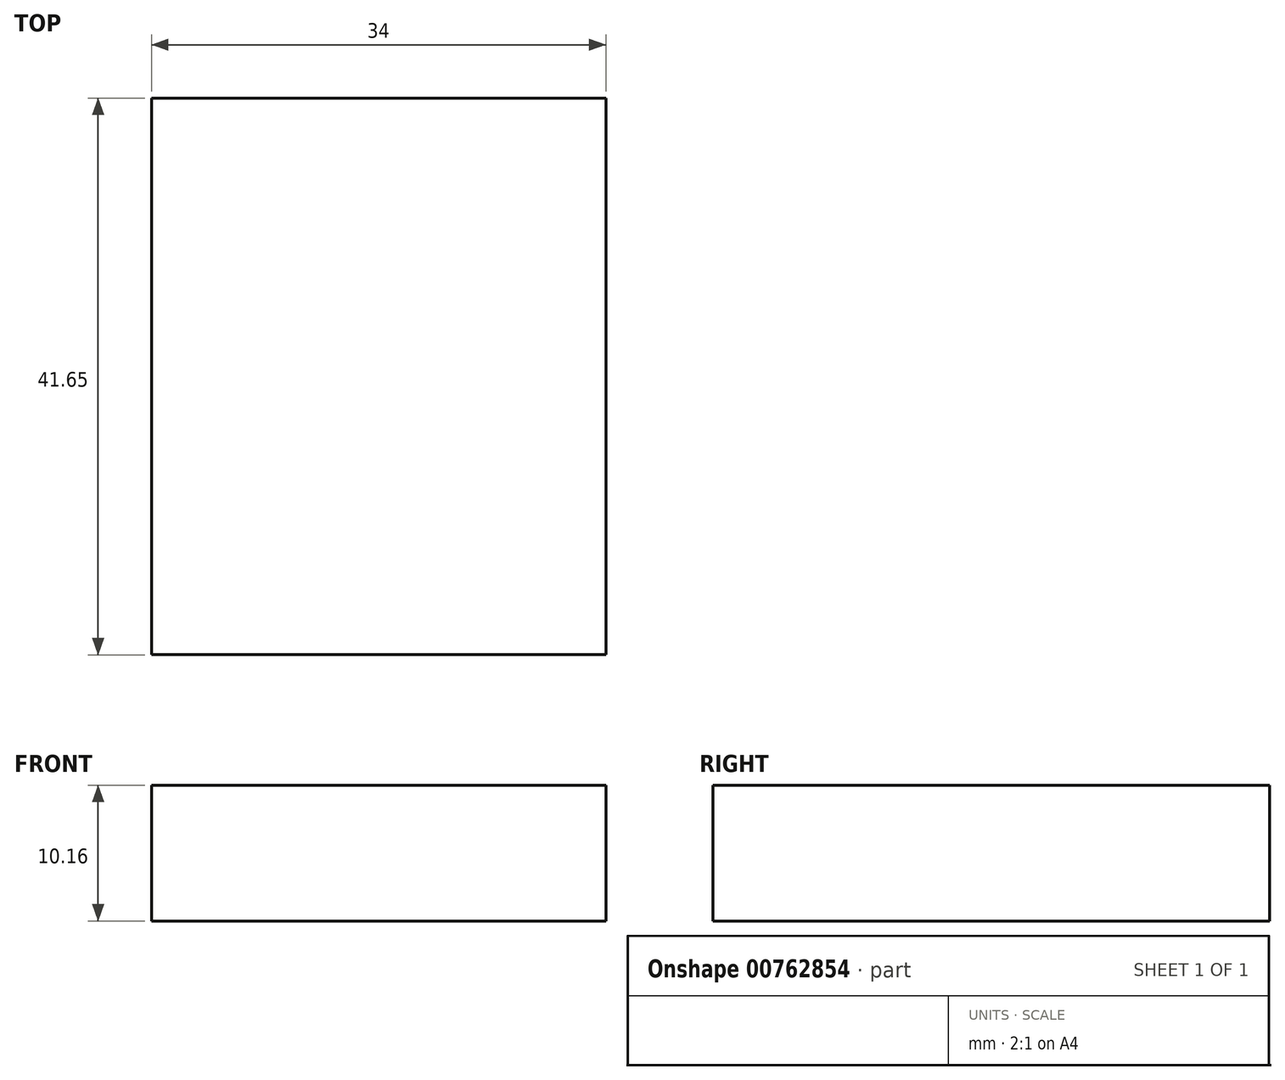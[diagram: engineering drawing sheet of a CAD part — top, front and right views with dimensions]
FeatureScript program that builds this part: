
annotation { "Feature Type Name" : "Feature", "Feature Type Description" : "" }
export const myFeature = defineFeature(function(context is Context, id is Id, definition is map)
    precondition{}
    {
        {
            var Q0;
            Q0=qCreatedBy(makeId("Top.planeOp"),FACE);
            var sketch = newSketch(context, id + "F0", { "sketchPlane" : qUnion([Q0])});
            skLineSegment(sketch, "E0", {"start": v(-67.43, -47.44) * mm, "end": v(-6.25, -47.44) * mm});
            skLineSegment(sketch, "E1", {"start": v(-6.25, -47.44) * mm, "end": v(-6.25, 18.3) * mm});
            skLineSegment(sketch, "E2", {"start": v(-6.25, 18.3) * mm, "end": v(-67.43, 18.3) * mm});
            skLineSegment(sketch, "E3", {"start": v(-67.43, 18.3) * mm, "end": v(-67.43, -47.44) * mm});
            skLineSegment(sketch, "E4.bottom", {"start": v(-133.43, 10.53) * mm, "end": v(-99.43, 10.53) * mm});
            skLineSegment(sketch, "E4.top", {"start": v(-133.43, 52.18) * mm, "end": v(-99.43, 52.18) * mm});
            skLineSegment(sketch, "E4.left", {"start": v(-133.43, 10.53) * mm, "end": v(-133.43, 52.18) * mm});
            skLineSegment(sketch, "E4.right", {"start": v(-99.43, 10.53) * mm, "end": v(-99.43, 52.18) * mm});
            skSolve(sketch);
        }
        {
            var Q0;
            Q0=makeQuery(id+"F0.imprint","IMPRINT",FACE,{"disambiguationData":[TD([[makeQuery(id+"F0.imprint","IMPRINT",EDGE,{"derivedFrom":sQuery(id+"F0.wireOp",EDGE,"E4.bottom")}),1.0]])]});
            extrude(context, id + "F1", {"entities" : qUnion([Q0]), "depth" : 10.16 * mm, "offsetDistance" : 25.4 * mm});
        }
    });
